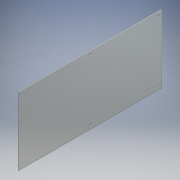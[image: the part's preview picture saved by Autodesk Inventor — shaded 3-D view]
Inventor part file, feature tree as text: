
AUTODESK INVENTOR PART (.ipt)
format: ipt  version: 2016 (Build 200138000, 138)  size: 108,544 bytes
history: native  units: mm
features: sketch x2, extrude x1, hole x1
ambient origin geometry x8: Origin, YZ Plane, XZ Plane, XY Plane, X Axis, Y Axis, Z Axis, Center Point
bodies: Solid1 (feature_tree)
feature tree (4):
  extrude  "Extrusion1"  Depth=190.0mm
  hole  "Hole1"  [1 undecoded]
  sketch  "Sketch1"  dims[d0=400.0mm d1=190.0mm]
  sketch  "Sketch2"  dims[d2=1.5875mm d3=0.0mm d4=10.0mm d5=10.0mm d6=10.0mm d7=10.0mm d8=10.0mm d9=5.5mm d10=6.0mm d11=10.4mm d12=2.0mm d13=90.0deg d14=8.0mm d15=20.594885mm]
note: 1 required parameter value undecoded (feature->parameter linkage not recoverable at this tier; creation-order binding heuristic only, values carry confidence <= 0.55)
